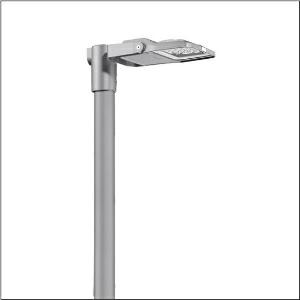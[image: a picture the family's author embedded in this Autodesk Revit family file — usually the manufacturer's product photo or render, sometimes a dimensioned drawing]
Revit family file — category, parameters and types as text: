
# Revit family: floodlight_fl_21_iq_micro___pl33t_5xa7761a4f3a_749b
name_source: partatom
category: Lighting Fixtures
units: mm (PartAtom-declared; Revit-internal decimal feet)

## family parameters
Cut with Voids When Loaded = No
Host = Face
Light Source = No
Part Type = Normal
Room Calculation Point = No
Round Connector Dimension = Use Diameter
Shared = No

## types (1)
- --- (1 x LED, 3050 lm, 23.1 W, 4000K)
    Apparent Load = 23 VA
    CIE Flux Codes = 26 75 99 100 100
    Color Rendering = 70
    Color Temperature = 4000K
    Default Elevation = 1800 mm
    Description = Floodlight FL 21 iQ micro, floodlight, primary light control with lens, of PMMA, primary optical cover: protective disc, of toughened safety glass, transparent, light distribution: PL33T, light emission: direct distribution, installation type: surface-mounted, LED, High Power LED, rated luminous flux: 3.050lm, luminous efficacy: 132lm/W, light colour: 740, colour temperature: 4000K, control: optimised constant luminous flux control (CLO 2.0), Desk-Remote (wireless, voltage-free reading and setting of iQ features in the workshop via application-optimized NFC function/RFID function), Light-Fading, Smart-Wire, Night-Set, Lumen-Switch, Temp-Guard, Auto-Match, with terminal, 6-pole, mains connection: 220..240V, AC, 50/60Hz, start of lifetime: 23W, end of service life: 24W, reduction: 11W, luminaire housing, of diecast aluminium, powder-coated, Siteco® metallic grey (DB 702S), corrosivity category C5 mid according to DIN EN ISO 12944, sealing non-destructively replaceable, please order mast flange separately, mast bracket, of steel, galvanised, powder-coated, Siteco® metallic grey (DB 702S), protection rating (complete): IP66, insulation class (complete): insulation class II (safety insulation), certification: CE, ENEC, VDE, protection symbol: D, impact resistance: IK07, permissible operating ambient temperature: -40..+40°C, permissible operating ambient temperature for outdoor applications: -40..+50°C, standard: DIN EN 12944, LABS conformity tested according to VDMA 24364:2018-05, packaging unit: 1 piece

Light Distribution: PL33T
    Height = 65 mm
    Lamp = 1 x LED
    Lamp Light Flux = 3050 lm
    Lamp Power = 23.1 W
    Lamp count = 1
    Length = 312 mm
    Luminous efficacy = 132 lm/W
    Manufacturer = Siteco
    ModVariant = No
    Model = 5XA7761A4F3A
    Number of Poles = 1
    OnlyDefault = Yes
    Power Factor = 1
    Product Name = Floodlight FL 21 iQ micro | PL33T
    Product group = floodlight | pylon annexe
    ProductGroupID = 6200
    Protection Class = Protection class II
    Protection Degree = IP 66
    RLX_Detail_Level = 1
    RLX_Emergency_Light_Flux = 0 lm
    RLX_Emergency_Type = 0
    RLX_Emergency_Type_DB = No
    RlxData = <blob elided: 101733 chars, md5=16e8ddb8>
    Socket = socket
    Standby Power = 0 W
    System Light Flux = 3050 lm
    System Power = 23 W
    Type Comments = factory setting: luminous flux: 100 % | dim-lin: 254 | 455 mA
    Type Image = l_1007121.jpg
    URL = http://relux.com
    VarID = @adj_098275
    Voltage = 0 V
    Weight = 0.00 kg
    Width = 230 mm

## geometry (parser evidence)
native form markers: Blend x4, Sweep x13
no freeform markers — native parametric forms only
